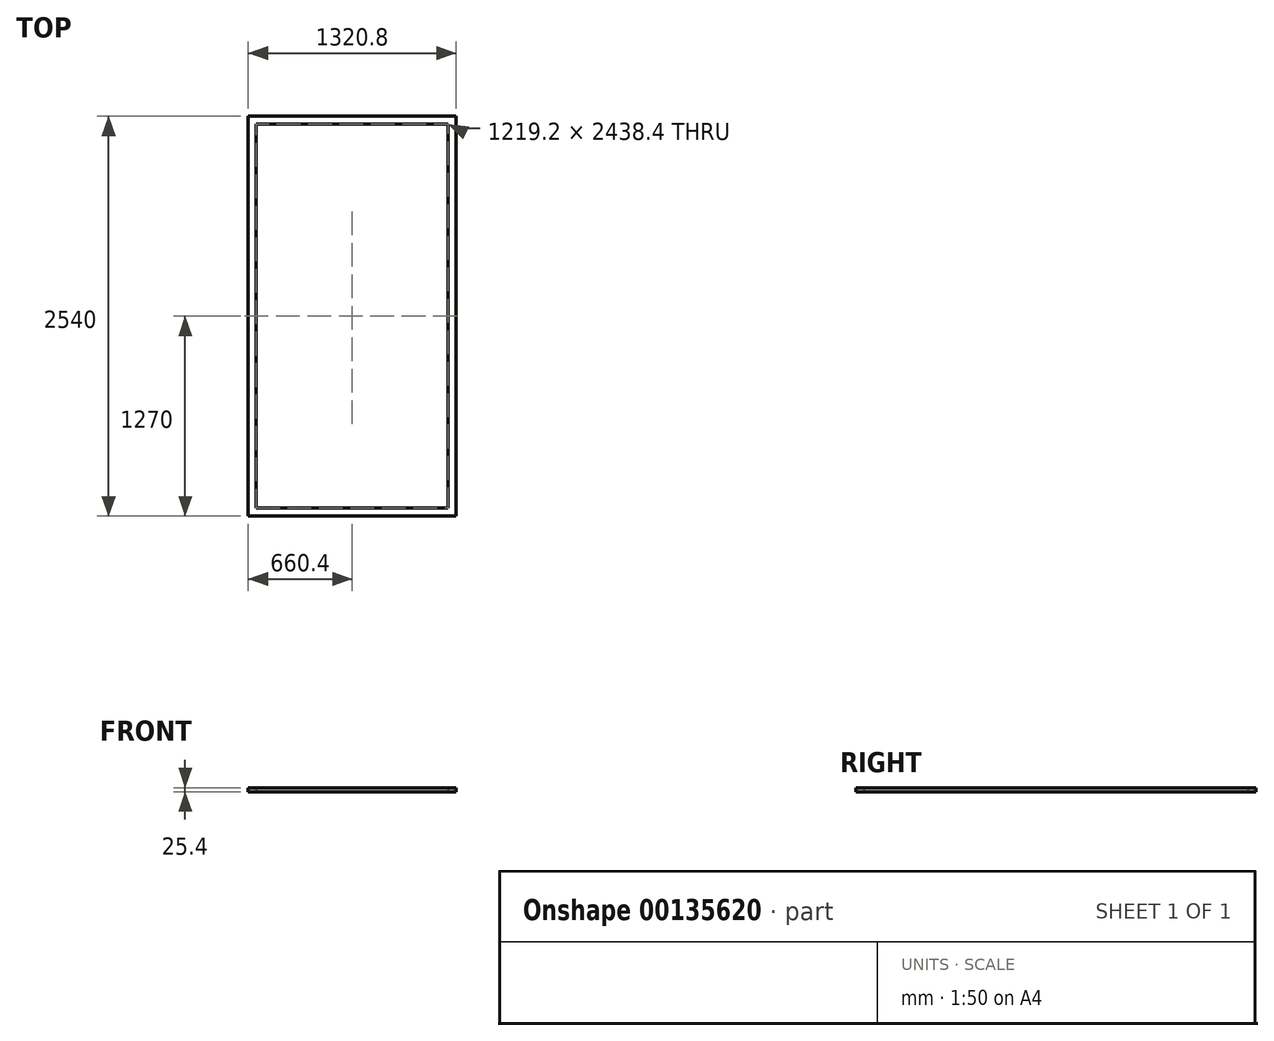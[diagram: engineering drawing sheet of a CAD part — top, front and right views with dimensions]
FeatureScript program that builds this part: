
annotation { "Feature Type Name" : "Feature", "Feature Type Description" : "" }
export const myFeature = defineFeature(function(context is Context, id is Id, definition is map)
    precondition{}
    {
        {
            var Q0;
            Q0=qCreatedBy(makeId("Top.planeOp"),FACE);
            var sketch = newSketch(context, id + "F0", { "sketchPlane" : qUnion([Q0])});
            skLineSegment(sketch, "E0.bottom", {"start": v(609.6, 1219.2) * mm, "end": v(-609.6, 1219.2) * mm});
            skLineSegment(sketch, "E0.top", {"start": v(609.6, -1219.2) * mm, "end": v(-609.6, -1219.2) * mm});
            skLineSegment(sketch, "E0.left", {"start": v(609.6, 1219.2) * mm, "end": v(609.6, -1219.2) * mm});
            skLineSegment(sketch, "E0.right", {"start": v(-609.6, 1219.2) * mm, "end": v(-609.6, -1219.2) * mm});
            skPoint(sketch, "E0.middle", {"position": v(0, 0) * mm});
            skLineSegment(sketch, "E1.0", {"start": v(660.4, 1270) * mm, "end": v(-660.4, 1270) * mm});
            skLineSegment(sketch, "E1.1", {"start": v(660.4, 1270) * mm, "end": v(660.4, -1270) * mm});
            skLineSegment(sketch, "E1.2", {"start": v(660.4, -1270) * mm, "end": v(-660.4, -1270) * mm});
            skLineSegment(sketch, "E1.3", {"start": v(-660.4, 1270) * mm, "end": v(-660.4, -1270) * mm});
            skSolve(sketch);
        }
        {
            var Q0;
            Q0=makeQuery(id+"F0.imprint","IMPRINT",FACE,{"disambiguationData":[TD([[makeQuery(id+"F0.imprint","IMPRINT",EDGE,{"derivedFrom":sQuery(id+"F0.wireOp",EDGE,"E0.bottom")}),-1.0]])]});
            extrude(context, id + "F1", {"entities" : qUnion([Q0]), "depth" : 25.4 * mm});
        }
    });
